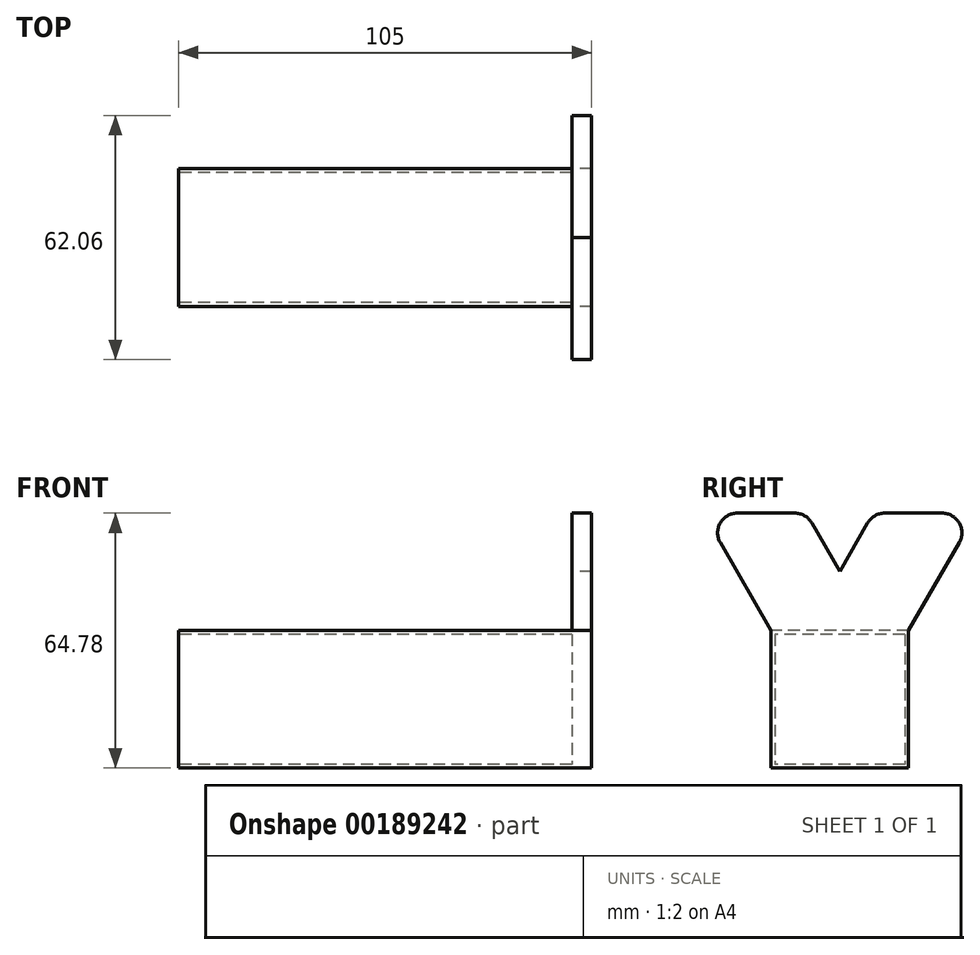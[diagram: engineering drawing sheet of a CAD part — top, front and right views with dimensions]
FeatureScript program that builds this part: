
annotation { "Feature Type Name" : "Feature", "Feature Type Description" : "" }
export const myFeature = defineFeature(function(context is Context, id is Id, definition is map)
    precondition{}
    {
        {
            var Q0;
            Q0=qCreatedBy(makeId("Right.planeOp"),FACE);
            var sketch = newSketch(context, id + "F0", { "sketchPlane" : qUnion([Q0])});
            skLineSegment(sketch, "E0.bottom", {"start": v(17.5, 17.5) * mm, "end": v(-17.5, 17.5) * mm});
            skLineSegment(sketch, "E0.top", {"start": v(17.5, -17.5) * mm, "end": v(-17.5, -17.5) * mm});
            skLineSegment(sketch, "E0.left", {"start": v(17.5, 17.5) * mm, "end": v(17.5, -17.5) * mm});
            skLineSegment(sketch, "E0.right", {"start": v(-17.5, 17.5) * mm, "end": v(-17.5, -17.5) * mm});
            skPoint(sketch, "E0.middle", {"position": v(0, 0) * mm});
            skLineSegment(sketch, "E1.bottom", {"start": v(16.5, 16.5) * mm, "end": v(-16.5, 16.5) * mm});
            skLineSegment(sketch, "E1.top", {"start": v(16.5, -16.5) * mm, "end": v(-16.5, -16.5) * mm});
            skLineSegment(sketch, "E1.left", {"start": v(16.5, 16.5) * mm, "end": v(16.5, -16.5) * mm});
            skLineSegment(sketch, "E1.right", {"start": v(-16.5, 16.5) * mm, "end": v(-16.5, -16.5) * mm});
            skSolve(sketch);
        }
        {
            var Q0;
            Q0 = qSketchRegion(id + "F0", true);
            extrude(context, id + "F1", {"entities" : qUnion([Q0]), "depth" : 100 * mm});
        }
        {
            var Q0;
            Q0=makeQuery(id+"F1.opExtrude","CAP_FACE",FACE,{"disambiguationData":[OSD([sQuery(id+"F0.wireOp",EDGE,"E0.bottom"),sQuery(id+"F0.wireOp",EDGE,"E0.top"),sQuery(id+"F0.wireOp",EDGE,"E0.left"),sQuery(id+"F0.wireOp",EDGE,"E0.right"),sQuery(id+"F0.wireOp",EDGE,"E1.bottom"),sQuery(id+"F0.wireOp",EDGE,"E1.top"),sQuery(id+"F0.wireOp",EDGE,"E1.left"),sQuery(id+"F0.wireOp",EDGE,"E1.right")])],"isStart":false});
            var sketch = newSketch(context, id + "F2", { "sketchPlane" : qUnion([Q0])});
            skLineSegment(sketch, "E2", {"start": v(-17.5, -17.5) * mm, "end": v(17.5, -17.5) * mm});
            skLineSegment(sketch, "E3", {"start": v(17.5, -17.5) * mm, "end": v(17.5, 17.5) * mm});
            skLineSegment(sketch, "E4", {"start": v(17.5, 17.5) * mm, "end": v(30.37, 39.78) * mm});
            skLineSegment(sketch, "E5", {"start": v(26.03, 47.28) * mm, "end": v(11.42, 47.28) * mm});
            skLineSegment(sketch, "E6", {"start": v(7.1, 44.78) * mm, "end": v(0, 32.5) * mm});
            skLineSegment(sketch, "E7", {"start": v(0, 32.5) * mm, "end": v(-7.1, 44.78) * mm});
            skLineSegment(sketch, "E8", {"start": v(-11.42, 47.28) * mm, "end": v(-26.03, 47.28) * mm});
            skLineSegment(sketch, "E9", {"start": v(-30.37, 39.78) * mm, "end": v(-17.5, 17.5) * mm});
            skLineSegment(sketch, "E10", {"start": v(-17.5, 17.5) * mm, "end": v(-17.5, -17.5) * mm});
            skPoint(sketch, "E11.visualSharp", {"position": v(-8.53, 47.28) * mm});
            skArc(sketch, "E11.filletArc", {"start": v(-7.1, 44.78) * mm, "mid": v(-8.92, 46.61) * mm, "end": v(-11.42, 47.28) * mm});
            skPoint(sketch, "E12.visualSharp", {"position": v(8.53, 47.28) * mm});
            skArc(sketch, "E12.filletArc", {"start": v(11.42, 47.28) * mm, "mid": v(8.92, 46.61) * mm, "end": v(7.1, 44.78) * mm});
            skPoint(sketch, "E13.visualSharp", {"position": v(-34.7, 47.28) * mm});
            skArc(sketch, "E13.filletArc", {"start": v(-26.03, 47.28) * mm, "mid": v(-30.37, 44.78) * mm, "end": v(-30.37, 39.78) * mm});
            skPoint(sketch, "E14.visualSharp", {"position": v(34.7, 47.28) * mm});
            skArc(sketch, "E14.filletArc", {"start": v(30.37, 39.78) * mm, "mid": v(30.37, 44.78) * mm, "end": v(26.03, 47.28) * mm});
            skSolve(sketch);
        }
        {
            var Q0;
            Q0 = qSketchRegion(id + "F2", true);
            extrude(context, id + "F3", {"entities" : qUnion([Q0]), "operationType" : NewBodyOperationType.ADD, "depth" : 5 * mm});
        }
    });
